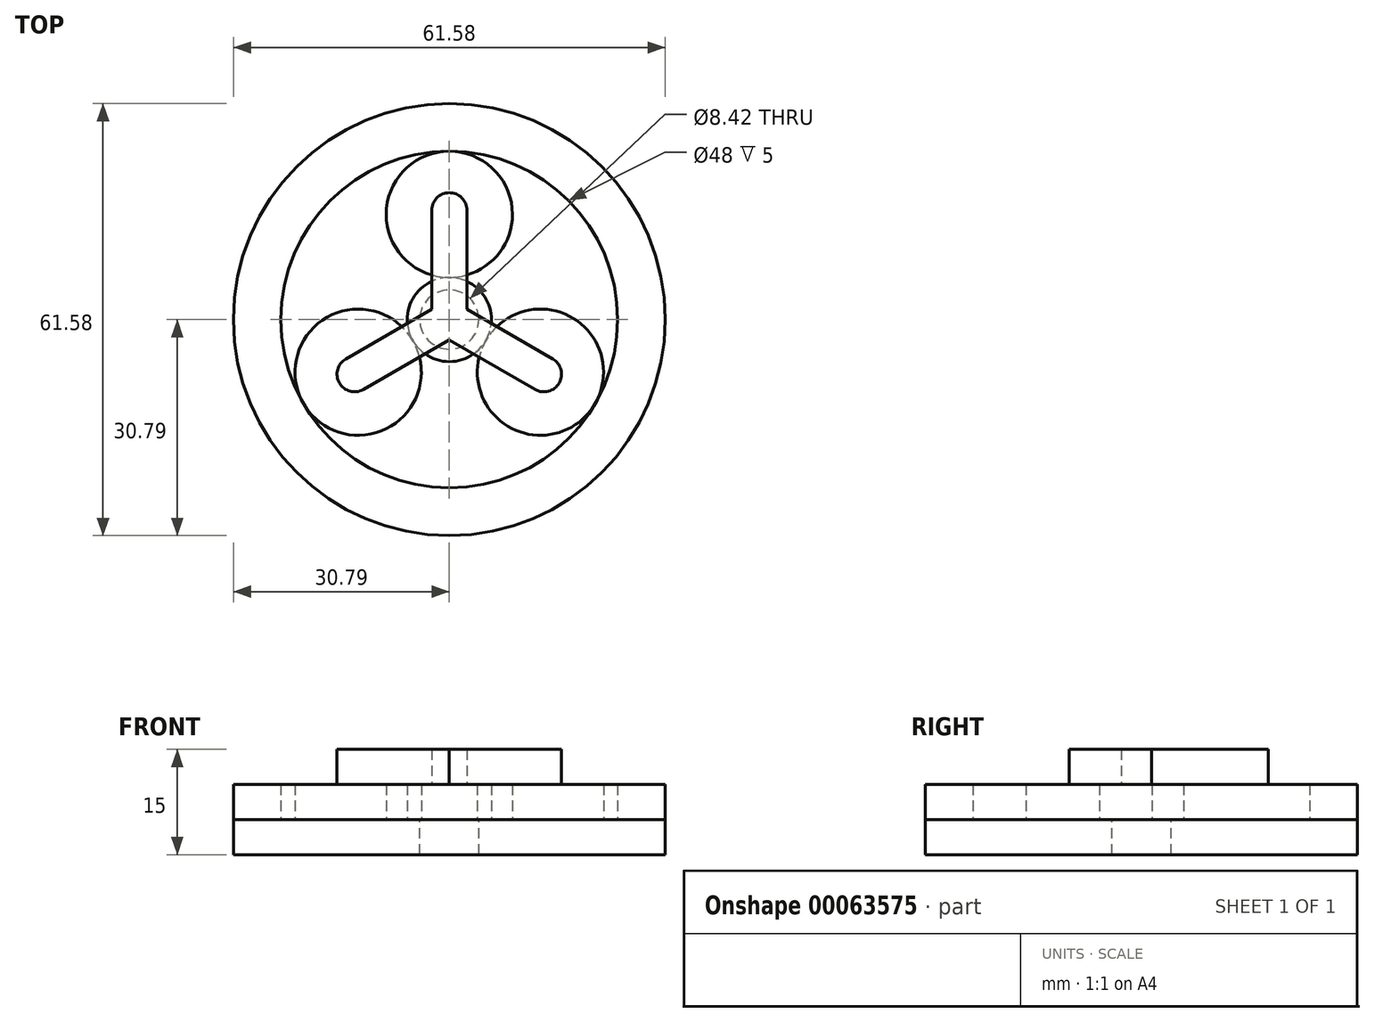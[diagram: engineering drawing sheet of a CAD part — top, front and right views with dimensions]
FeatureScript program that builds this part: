
annotation { "Feature Type Name" : "Feature", "Feature Type Description" : "" }
export const myFeature = defineFeature(function(context is Context, id is Id, definition is map)
    precondition{}
    {
        {
            var Q0;
            Q0=qCreatedBy(makeId("Top.planeOp"),FACE);
            var sketch = newSketch(context, id + "F0", { "sketchPlane" : qUnion([Q0])});
            skCircle(sketch, "E0", {"center": v(0, 0) * mm, "radius": 6 * mm});
            skCircle(sketch, "E1", {"center": v(0, 0) * mm, "radius": 24 * mm});
            skCircle(sketch, "E2", {"center": v(0, 15) * mm, "radius": 9 * mm});
            skCircle(sketch, "E3", {"center": v(0, 0) * mm, "radius": 30.79 * mm});
            skCircle(sketch, "E4.1.0", {"center": v(-13, -7.5) * mm, "radius": 9 * mm});
            skCircle(sketch, "E4.2.0", {"center": v(13, -7.5) * mm, "radius": 9 * mm});
            skSolve(sketch);
        }
        {
            var Q0;
            {var subQ0=sQuery(id+"F0.wireOp",EDGE,"E2");var subQ1=makeQuery(id+"F0.imprint","INTERSECT",VERTEX,{"derivedFrom":[sQuery(id+"F0.wireOp",EDGE,"E0"),subQ0]});Q0=makeQuery(id+"F0.imprint","IMPRINT",FACE,{"disambiguationData":[TD([[makeQuery(id+"F0.imprint","IMPRINT",EDGE,{"disambiguationData":[TD([[subQ1,1.0]])],"derivedFrom":subQ0}),1.0]])]});}
            var Q1;
            Q1=makeQuery(id+"F0.imprint","IMPRINT",FACE,{"disambiguationData":[TD([[makeQuery(id+"F0.imprint","IMPRINT",EDGE,{"derivedFrom":sQuery(id+"F0.wireOp",EDGE,"E0")}),1.0]])]});
            var Q2;
            Q2=makeQuery(id+"F0.imprint","IMPRINT",FACE,{"disambiguationData":[TD([[makeQuery(id+"F0.imprint","IMPRINT",EDGE,{"derivedFrom":sQuery(id+"F0.wireOp",EDGE,"E1")}),-1.0]])]});
            var Q3;
            {var subQ0=sQuery(id+"F0.wireOp",EDGE,"E4.1.0");var subQ1=makeQuery(id+"F0.imprint","INTERSECT",VERTEX,{"derivedFrom":[sQuery(id+"F0.wireOp",EDGE,"E0"),subQ0]});Q3=makeQuery(id+"F0.imprint","IMPRINT",FACE,{"disambiguationData":[TD([[makeQuery(id+"F0.imprint","IMPRINT",EDGE,{"disambiguationData":[TD([[subQ1,1.0]])],"derivedFrom":subQ0}),1.0]])]});}
            var Q4;
            {var subQ0=sQuery(id+"F0.wireOp",EDGE,"E4.2.0");var subQ1=makeQuery(id+"F0.imprint","INTERSECT",VERTEX,{"derivedFrom":[sQuery(id+"F0.wireOp",EDGE,"E0"),subQ0]});Q4=makeQuery(id+"F0.imprint","IMPRINT",FACE,{"disambiguationData":[TD([[makeQuery(id+"F0.imprint","IMPRINT",EDGE,{"disambiguationData":[TD([[subQ1,1.0]])],"derivedFrom":subQ0}),1.0]])]});}
            extrude(context, id + "F1", {"entities" : qUnion([Q0, Q1, Q2, Q3, Q4]), "depth" : 5 * mm});
        }
        {
            var Q0;
            Q0=makeQuery(id+"F1.opExtrude","CAP_FACE",FACE,{"disambiguationData":[OSD([sQuery(id+"F0.wireOp",EDGE,"E4.1.0")])],"isStart":false});
            var sketch = newSketch(context, id + "F2", { "sketchPlane" : qUnion([Q0])});
            skLineSegment(sketch, "E5", {"start": v(0, 0) * mm, "end": v(-2.51, 1.45) * mm, "construction": true});
            skLineSegment(sketch, "E6", {"start": v(-2.51, 1.45) * mm, "end": v(-2.51, 15.58) * mm});
            skLineSegment(sketch, "E7", {"start": v(0, 15.58) * mm, "end": v(0, 0) * mm, "construction": true});
            skLineSegment(sketch, "E8.MirrorCS", {"start": v(2.51, 1.45) * mm, "end": v(2.51, 15.58) * mm});
            skLineSegment(sketch, "E9.MirrorCS", {"start": v(0, 0) * mm, "end": v(2.51, 1.45) * mm, "construction": true});
            skArc(sketch, "E10", {"start": v(-2.51, 15.58) * mm, "mid": v(0, 18.1) * mm, "end": v(2.51, 15.58) * mm});
            skPoint(sketch, "E11.MirrorCS.start.orphan", {"position": v(2.51, 15.58) * mm});
            skArc(sketch, "E12.1.0", {"start": v(-12.24, -9.96) * mm, "mid": v(-15.67, -9.05) * mm, "end": v(-14.75, -5.62) * mm});
            skLineSegment(sketch, "E12.1.1", {"start": v(0, -2.9) * mm, "end": v(-12.24, -9.96) * mm});
            skLineSegment(sketch, "E12.1.2", {"start": v(-2.51, 1.45) * mm, "end": v(-14.75, -5.62) * mm});
            skArc(sketch, "E12.2.0", {"start": v(14.75, -5.62) * mm, "mid": v(15.67, -9.05) * mm, "end": v(12.24, -9.96) * mm});
            skLineSegment(sketch, "E12.2.1", {"start": v(2.51, 1.45) * mm, "end": v(14.75, -5.62) * mm});
            skLineSegment(sketch, "E12.2.2", {"start": v(0, -2.9) * mm, "end": v(12.24, -9.96) * mm});
            skPoint(sketch, "E12.center", {"position": v(0, 0) * mm});
            skSolve(sketch);
        }
        {
            var Q0;
            Q0 = qSketchRegion(id + "F2", true);
            extrude(context, id + "F3", {"entities" : qUnion([Q0]), "depth" : 5 * mm});
        }
        {
            var Q0;
            Q0=makeQuery(id+"F0.imprint","IMPRINT",FACE,{"disambiguationData":[TD([[makeQuery(id+"F0.imprint","IMPRINT",EDGE,{"derivedFrom":sQuery(id+"F0.wireOp",EDGE,"E3")}),1.0]])]});
            var sketch = newSketch(context, id + "F4", { "sketchPlane" : qUnion([Q0])});
            skCircle(sketch, "E13.0", {"center": v(0, 0) * mm, "radius": 30.79 * mm});
            skCircle(sketch, "E14", {"center": v(0, 0) * mm, "radius": 4.21 * mm});
            skSolve(sketch);
        }
        {
            var Q0;
            Q0 = qSketchRegion(id + "F4", true);
            extrude(context, id + "F5", {"entities" : qUnion([Q0]), "oppositeDirection" : true, "depth" : 5 * mm});
        }
    });
